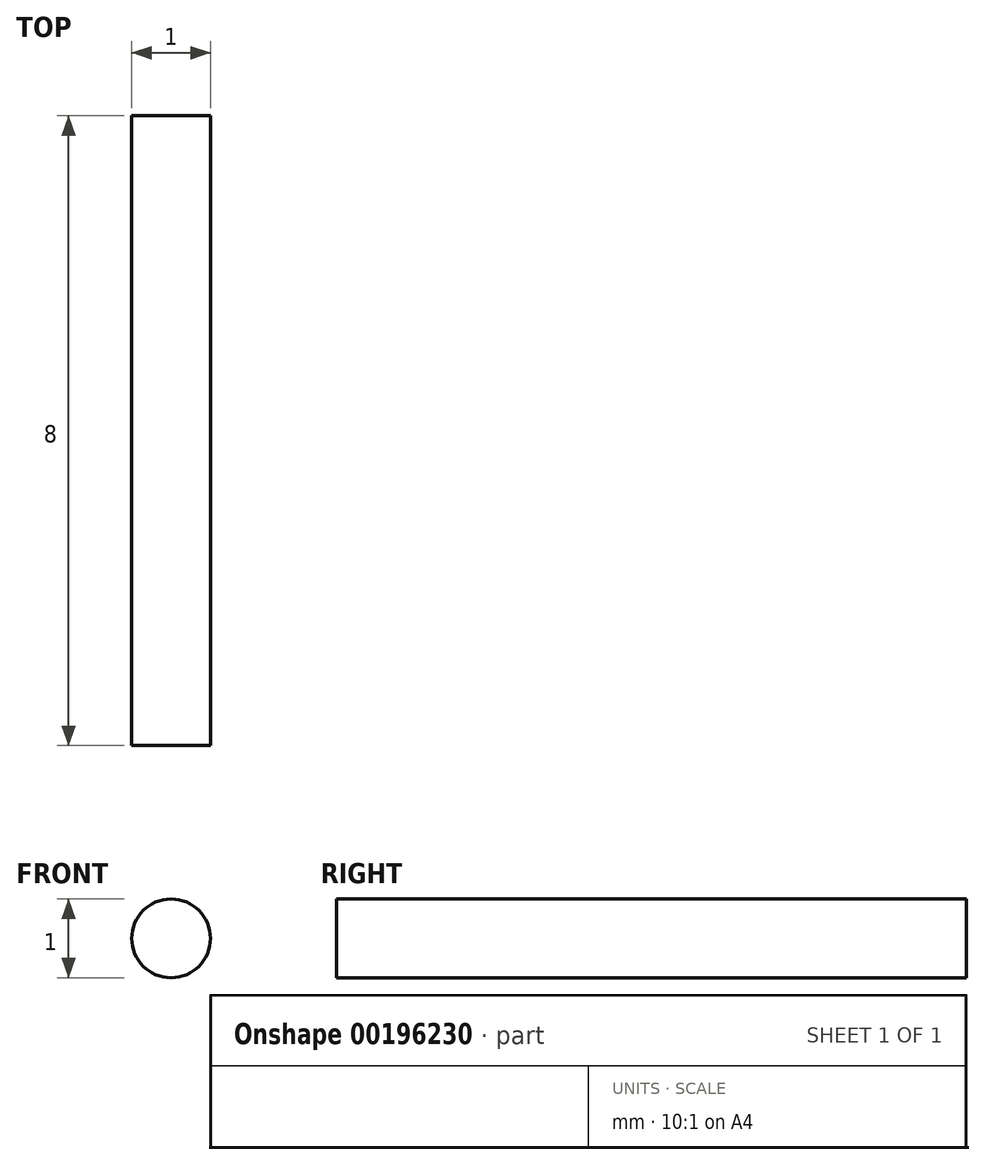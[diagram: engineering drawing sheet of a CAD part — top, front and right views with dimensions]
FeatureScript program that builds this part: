
annotation { "Feature Type Name" : "Feature", "Feature Type Description" : "" }
export const myFeature = defineFeature(function(context is Context, id is Id, definition is map)
    precondition{}
    {
        {
            var Q0;
            Q0=qCreatedBy(makeId("Front.planeOp"),FACE);
            var sketch = newSketch(context, id + "F0", { "sketchPlane" : qUnion([Q0])});
            skCircle(sketch, "E0", {"center": v(0, 0) * mm, "radius": 0.5 * mm});
            skSolve(sketch);
        }
        {
            var Q0;
            Q0 = qSketchRegion(id + "F0", true);
            extrude(context, id + "F1", {"entities" : qUnion([Q0]), "depth" : 8 * mm});
        }
    });
